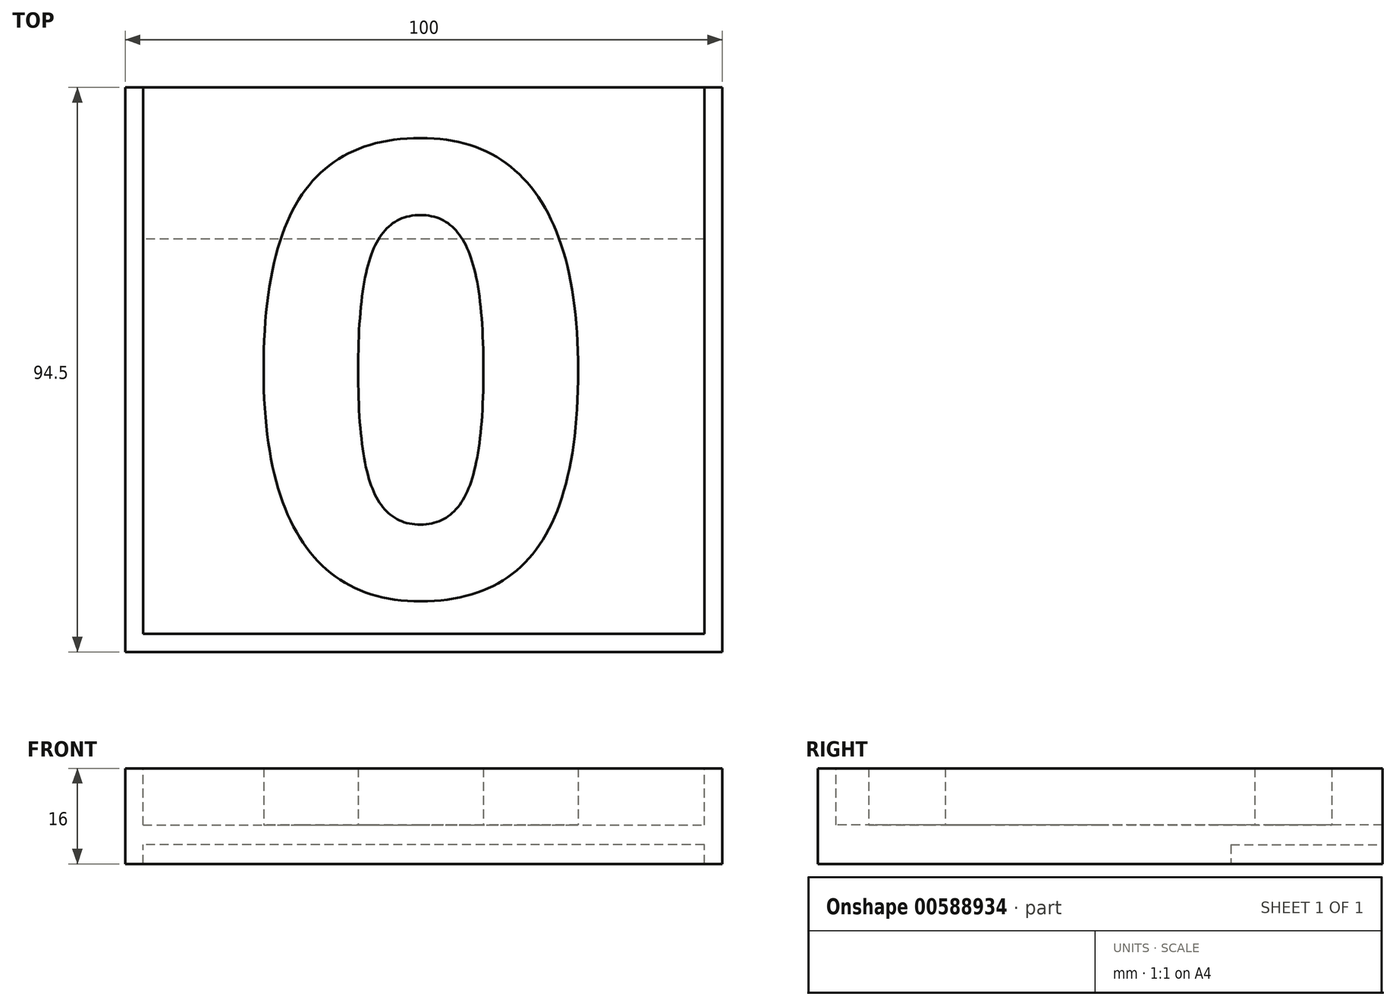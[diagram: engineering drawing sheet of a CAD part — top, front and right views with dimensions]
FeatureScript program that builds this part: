
annotation { "Feature Type Name" : "Feature", "Feature Type Description" : "" }
export const myFeature = defineFeature(function(context is Context, id is Id, definition is map)
    precondition{}
    {
        {
            var Q0;
            Q0=qCreatedBy(makeId("Top.planeOp"),FACE);
            var sketch = newSketch(context, id + "F0", { "sketchPlane" : qUnion([Q0])});
            skLineSegment(sketch, "E0.bottom", {"start": v(0, 0) * mm, "end": v(100, 0) * mm});
            skLineSegment(sketch, "E0.top", {"start": v(0, 91.5) * mm, "end": v(100, 91.5) * mm});
            skLineSegment(sketch, "E0.left", {"start": v(0, 0) * mm, "end": v(0, 91.5) * mm});
            skLineSegment(sketch, "E0.right", {"start": v(100, 0) * mm, "end": v(100, 91.5) * mm});
            skSolve(sketch);
        }
        {
            var Q0;
            Q0=qSketchRegion(id+"F0",true);
            extrude(context, id + "F1", {"entities" : qUnion([Q0]), "depth" : 16 * mm});
        }
        {
            var Q0;
            Q0=makeQuery(id+"F1.opExtrude","CAP_FACE",FACE,{"disambiguationData":[OSD([sQuery(id+"F0.wireOp",EDGE,"E0.bottom"),sQuery(id+"F0.wireOp",EDGE,"E0.top"),sQuery(id+"F0.wireOp",EDGE,"E0.left"),sQuery(id+"F0.wireOp",EDGE,"E0.right")])],"isStart":false});
            var sketch = newSketch(context, id + "F2", { "sketchPlane" : qUnion([Q0])});
            skLineSegment(sketch, "E1.bottom", {"start": v(3, 91.5) * mm, "end": v(97, 91.5) * mm});
            skLineSegment(sketch, "E1.top", {"start": v(3, 0) * mm, "end": v(97, 0) * mm});
            skLineSegment(sketch, "E1.left", {"start": v(3, 91.5) * mm, "end": v(3, 0) * mm});
            skLineSegment(sketch, "E1.right", {"start": v(97, 91.5) * mm, "end": v(97, 0) * mm});
            skSolve(sketch);
        }
        {
            var Q0;
            Q0=qSketchRegion(id+"F2",true);
            extrude(context, id + "F3", {"entities" : qUnion([Q0]), "operationType" : NewBodyOperationType.REMOVE, "oppositeDirection" : true, "depth" : 9.5 * mm});
        }
        {
            var Q0;
            Q0=makeQuery(id+"F1.opExtrude","CAP_FACE",FACE,{"disambiguationData":[OSD([sQuery(id+"F0.wireOp",EDGE,"E0.bottom"),sQuery(id+"F0.wireOp",EDGE,"E0.top"),sQuery(id+"F0.wireOp",EDGE,"E0.left"),sQuery(id+"F0.wireOp",EDGE,"E0.right")])],"isStart":true});
            var sketch = newSketch(context, id + "F4", { "sketchPlane" : qUnion([Q0])});
            skLineSegment(sketch, "E2.bottom", {"start": v(97, -66.1) * mm, "end": v(3, -66.1) * mm});
            skLineSegment(sketch, "E2.top", {"start": v(97, -94.1) * mm, "end": v(3, -94.1) * mm});
            skLineSegment(sketch, "E2.left", {"start": v(97, -66.1) * mm, "end": v(97, -94.1) * mm});
            skLineSegment(sketch, "E2.right", {"start": v(3, -66.1) * mm, "end": v(3, -94.1) * mm});
            skSolve(sketch);
        }
        {
            var Q0;
            Q0=qSketchRegion(id+"F4",true);
            extrude(context, id + "F5", {"entities" : qUnion([Q0]), "operationType" : NewBodyOperationType.REMOVE, "oppositeDirection" : true, "depth" : 3.2 * mm});
        }
        {
            var Q0;
            Q0=makeQuery(id+"F3.boolean.opBoolean","COPY",FACE,{"derivedFrom":makeQuery(id+"F3.opExtrude","CAP_FACE",FACE,{"disambiguationData":[OSD([sQuery(id+"F2.wireOp",EDGE,"E1.bottom"),sQuery(id+"F2.wireOp",EDGE,"E1.top"),sQuery(id+"F2.wireOp",EDGE,"E1.left"),sQuery(id+"F2.wireOp",EDGE,"E1.right")])],"isStart":false})});
            var sketch = newSketch(context, id + "F6", { "sketchPlane" : qUnion([Q0])});
            skText(sketch, "E3", { "text": "0", "fontName": "OpenSans-Bold.ttf"});
            const initialGuessF6  = {"E3": [0.01937, 0.0065, 1, 0, 0.076]};
            skSetInitialGuess(sketch, initialGuessF6);
            skSolve(sketch);
        }
        {
            var Q0;
            Q0=qSketchRegion(id+"F6",true);
            extrude(context, id + "F7", {"entities" : qUnion([Q0]), "operationType" : NewBodyOperationType.ADD, "depth" : 9.5 * mm});
        }
        {
            var Q0;
            Q0=makeQuery(id+"F1.opExtrude","SWEPT_FACE",FACE,{"disambiguationData":[OSD([sQuery(id+"F0.wireOp",EDGE,"E0.bottom")])]});
            var sketch = newSketch(context, id + "F8", { "sketchPlane" : qUnion([Q0])});
            skLineSegment(sketch, "E4.bottom", {"start": v(0, 16) * mm, "end": v(100, 16) * mm});
            skLineSegment(sketch, "E4.top", {"start": v(0, 0) * mm, "end": v(100, 0) * mm});
            skLineSegment(sketch, "E4.left", {"start": v(0, 16) * mm, "end": v(0, 0) * mm});
            skLineSegment(sketch, "E4.right", {"start": v(100, 16) * mm, "end": v(100, 0) * mm});
            skSolve(sketch);
        }
        {
            var Q0;
            Q0 = qSketchRegion(id + "F8", true);
            extrude(context, id + "F9", {"entities" : qUnion([Q0]), "operationType" : NewBodyOperationType.ADD, "depth" : 3 * mm, "offsetDistance" : 25 * mm});
        }
    });
